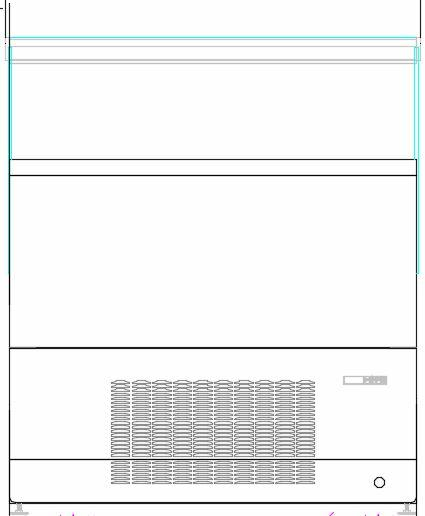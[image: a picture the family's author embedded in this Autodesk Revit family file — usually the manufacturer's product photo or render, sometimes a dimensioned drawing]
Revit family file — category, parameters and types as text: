
# Revit family: QF_OSCARTEK_VENTURA_G1110_cat
name_source: partatom
category: Specialty Equipment
units: mm (PartAtom-declared; Revit-internal decimal feet)

## family parameters
Always vertical = Yes
Cut with Voids When Loaded = No
Enable Cutting in Views = No
Maintain Annotation Orientation = No
Part Type = Normal
Room Calculation Point = No
Round Connector Dimension = Use Diameter
Shared = No
Work Plane-Based = No

## types (1)
- QF_OSCARTEK_VENTURA_G1110_cat
    Apparent Power = 1082 VA
    BTUH = 6240.0 Btu/h
    Conn Conduit = Yes
    Cycle = 50 Hz
    Default Elevation = 0"
    Depth = 44 15/16"
    Description = GELATO CASE
    Elec Conn Connection Height = 0"
    Elec Conn RI Height = 0"
    FL Amps = 5 A
    Foodservice Equipment Identifier = Yes
    Height = 51 3/16"
    Identify Quantity as Lot = Yes
    Indirect Waste Connection Height = 0"
    Indirect Waste Flow = 0 GPM
    Indirect Waste Size = 1"
    Length = 43 11/16"
    Manufacturer = OSCARTEK
    Max Overcurrent Protection = 0 A
    Min Ckt Ampacity = 0 A
    Model = VENTURA G1110
    Number of Poles = 1
    Phase = 1
    Refrigerant Type = R404A
    Refrigerant Volume = 0.00 kip
    Volts = 208 V
    Waste Water Discharge Temperature = 0 °F
    Watts = 1950 W
    Weight in Pounds = 540

## geometry (parser evidence)
native form markers: Blend x8, Sweep x11
no freeform markers — native parametric forms only
